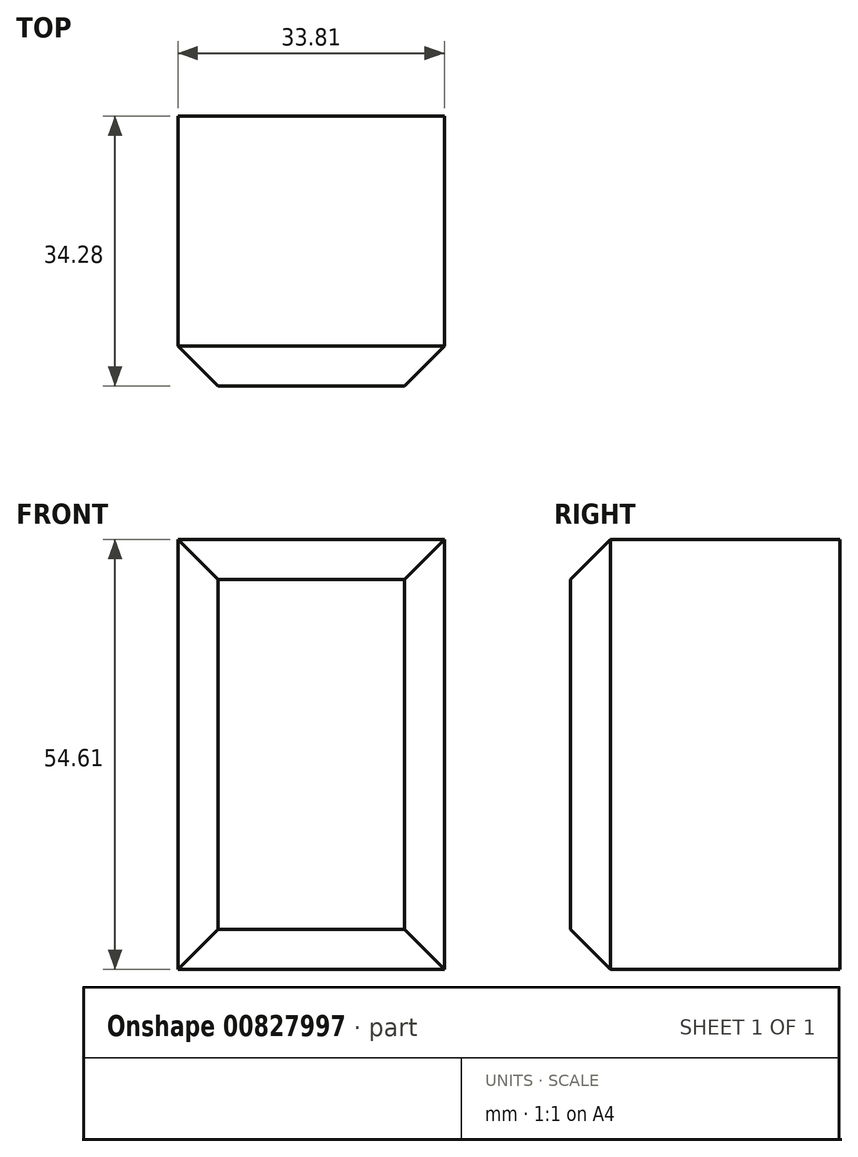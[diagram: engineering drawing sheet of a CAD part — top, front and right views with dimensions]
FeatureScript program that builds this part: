
annotation { "Feature Type Name" : "Feature", "Feature Type Description" : "" }
export const myFeature = defineFeature(function(context is Context, id is Id, definition is map)
    precondition{}
    {
        {
            var Q0;
            Q0=qCreatedBy(makeId("Top.planeOp"),FACE);
            var sketch = newSketch(context, id + "F0", { "sketchPlane" : qUnion([Q0])});
            skLineSegment(sketch, "E0.bottom", {"start": v(-65.34, -57.19) * mm, "end": v(-31.53, -57.19) * mm});
            skLineSegment(sketch, "E0.top", {"start": v(-65.34, -91.47) * mm, "end": v(-31.53, -91.47) * mm});
            skLineSegment(sketch, "E0.left", {"start": v(-65.34, -57.19) * mm, "end": v(-65.34, -91.47) * mm});
            skLineSegment(sketch, "E0.right", {"start": v(-31.53, -57.19) * mm, "end": v(-31.53, -91.47) * mm});
            skSolve(sketch);
        }
        {
            var Q0;
            Q0=makeQuery(id+"F0.imprint","IMPRINT",FACE,{"disambiguationData":[TD([[makeQuery(id+"F0.imprint","IMPRINT",EDGE,{"derivedFrom":sQuery(id+"F0.wireOp",EDGE,"E0.bottom")}),-1.0]])]});
            extrude(context, id + "F1", {"entities" : qUnion([Q0]), "depth" : 54.6 * mm, "offsetDistance" : 25.4 * mm});
        }
        {
            var Q0;
            Q0=makeQuery(id+"F1.opExtrude","CAP_EDGE",EDGE,{"disambiguationData":[OSD([sQuery(id+"F0.wireOp",EDGE,"E0.top")])],"isStart":false});
            var Q1;
            Q1=makeQuery(id+"F1.opExtrude","SWEPT_FACE",FACE,{"disambiguationData":[OSD([sQuery(id+"F0.wireOp",EDGE,"E0.top")])]});
            chamfer(context, id + "F2", {"entities" : qUnion([Q0, Q1]), "width" : 5.08 * mm, "tangentPropagation" : true});
        }
    });
